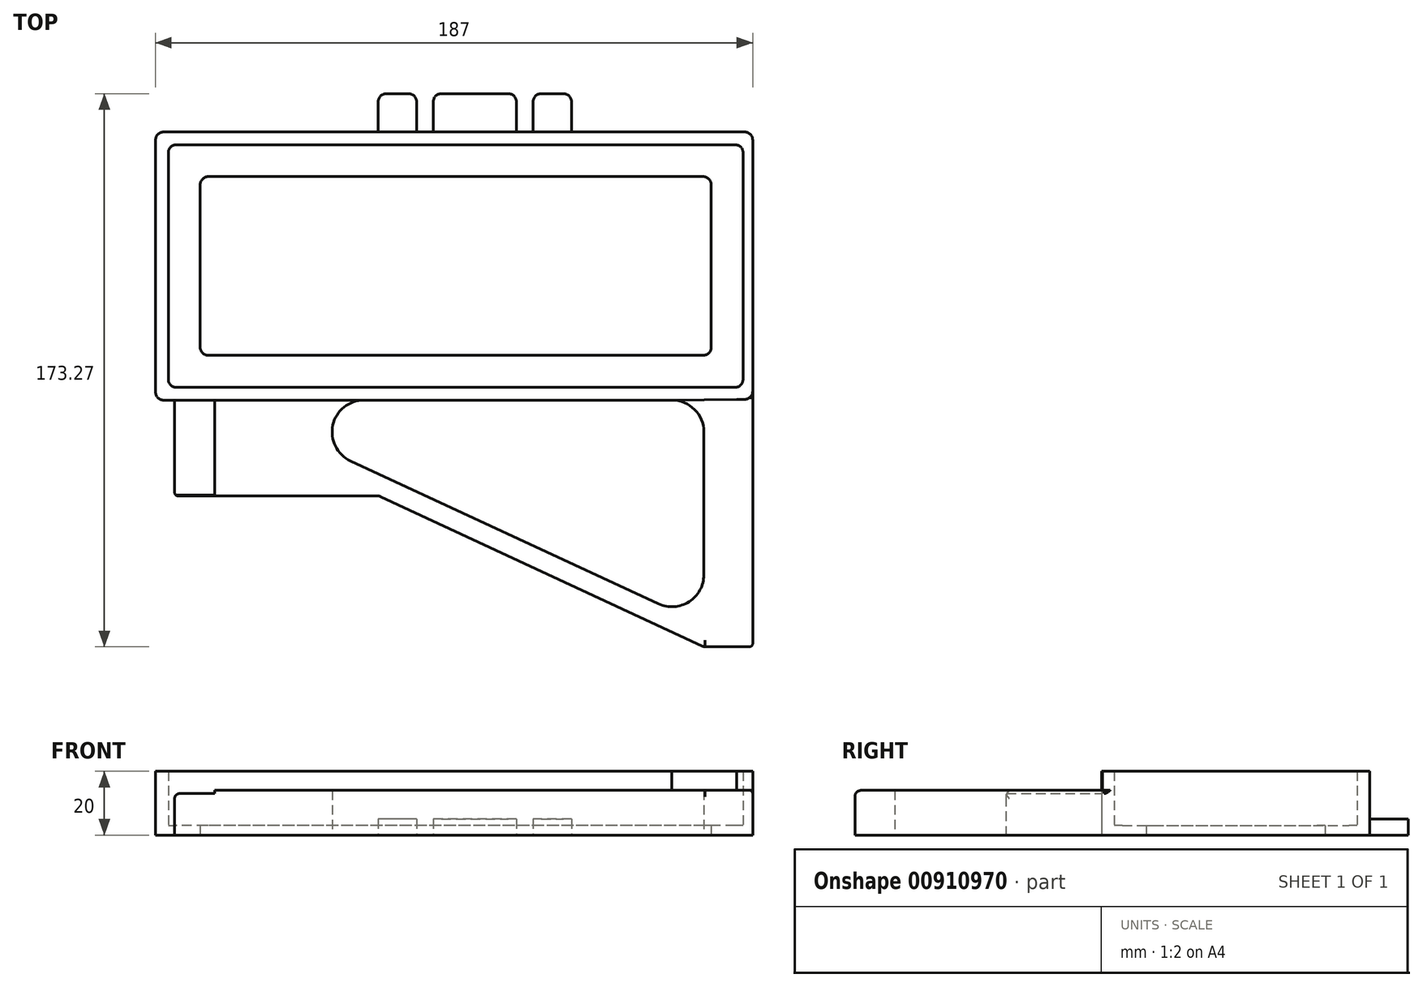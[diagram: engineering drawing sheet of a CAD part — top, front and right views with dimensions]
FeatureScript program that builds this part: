
annotation { "Feature Type Name" : "Feature", "Feature Type Description" : "" }
export const myFeature = defineFeature(function(context is Context, id is Id, definition is map)
    precondition{}
    {
        {
            var Q0;
            Q0=qCreatedBy(makeId("Top.planeOp"),FACE);
            var sketch = newSketch(context, id + "F0", { "sketchPlane" : qUnion([Q0])});
            skLineSegment(sketch, "E0.bottom", {"start": v(87.5, 0) * mm, "end": v(-87.5, 0) * mm});
            skLineSegment(sketch, "E0.top", {"start": v(87.5, 76) * mm, "end": v(-87.5, 76) * mm});
            skLineSegment(sketch, "E0.left", {"start": v(90, 2.5) * mm, "end": v(90, 73.5) * mm});
            skLineSegment(sketch, "E0.right", {"start": v(-90, 2.5) * mm, "end": v(-90, 73.5) * mm});
            skLineSegment(sketch, "E1.0", {"start": v(102, 80) * mm, "end": v(-74, 80) * mm});
            skLineSegment(sketch, "E2.0", {"start": v(-94, 0) * mm, "end": v(-94, 76) * mm});
            skLineSegment(sketch, "E3.0", {"start": v(67.7, -4) * mm, "end": v(-28.7, -4) * mm});
            skLineSegment(sketch, "E4.0", {"start": v(93, 0) * mm, "end": v(93, 76) * mm});
            skLineSegment(sketch, "E5", {"start": v(-74, 80) * mm, "end": v(-91.5, 80) * mm});
            skLineSegment(sketch, "E6", {"start": v(-94, 76) * mm, "end": v(-94, 77.5) * mm});
            skLineSegment(sketch, "E7", {"start": v(-94, -1.5) * mm, "end": v(-94, 0) * mm});
            skLineSegment(sketch, "E8", {"start": v(-88, -4) * mm, "end": v(-91.5, -4) * mm});
            skLineSegment(sketch, "E9", {"start": v(90.5, 80) * mm, "end": v(102, 80) * mm});
            skLineSegment(sketch, "E10", {"start": v(93, 77.5) * mm, "end": v(93, 76) * mm});
            skLineSegment(sketch, "E11", {"start": v(88, -3.77) * mm, "end": v(90.5, -3.77) * mm});
            skLineSegment(sketch, "E12", {"start": v(93, -1.27) * mm, "end": v(93, 0) * mm});
            skLineSegment(sketch, "E13", {"start": v(-7, 80) * mm, "end": v(-7, 89.5) * mm});
            skLineSegment(sketch, "E14", {"start": v(-4.5, 92) * mm, "end": v(16.5, 92) * mm});
            skLineSegment(sketch, "E15", {"start": v(19, 89.5) * mm, "end": v(19, 80) * mm});
            skLineSegment(sketch, "E16", {"start": v(6, 92) * mm, "end": v(6, 80) * mm, "construction": true});
            skLineSegment(sketch, "E17", {"start": v(6, 80) * mm, "end": v(6, 76) * mm, "construction": true});
            skLineSegment(sketch, "E18", {"start": v(-12.25, 80) * mm, "end": v(-12.25, 89.5) * mm});
            skLineSegment(sketch, "E19", {"start": v(-14.75, 92) * mm, "end": v(-21.75, 92) * mm});
            skLineSegment(sketch, "E20", {"start": v(-24.25, 89.5) * mm, "end": v(-24.25, 80) * mm});
            skLineSegment(sketch, "E21", {"start": v(24.25, 80) * mm, "end": v(24.25, 89.5) * mm});
            skLineSegment(sketch, "E22", {"start": v(26.75, 92) * mm, "end": v(33.75, 92) * mm});
            skLineSegment(sketch, "E23", {"start": v(36.25, 89.5) * mm, "end": v(36.25, 80) * mm});
            skPoint(sketch, "E24.visualSharp", {"position": v(19, 92) * mm});
            skArc(sketch, "E24.filletArc", {"start": v(19, 89.5) * mm, "mid": v(18.27, 91.27) * mm, "end": v(16.5, 92) * mm});
            skPoint(sketch, "E25.visualSharp", {"position": v(-7, 92) * mm});
            skArc(sketch, "E25.filletArc", {"start": v(-4.5, 92) * mm, "mid": v(-6.27, 91.27) * mm, "end": v(-7, 89.5) * mm});
            skPoint(sketch, "E26.visualSharp", {"position": v(-12.25, 92) * mm});
            skArc(sketch, "E26.filletArc", {"start": v(-12.25, 89.5) * mm, "mid": v(-12.98, 91.27) * mm, "end": v(-14.75, 92) * mm});
            skPoint(sketch, "E27.visualSharp", {"position": v(24.25, 92) * mm});
            skArc(sketch, "E27.filletArc", {"start": v(26.75, 92) * mm, "mid": v(24.98, 91.27) * mm, "end": v(24.25, 89.5) * mm});
            skPoint(sketch, "E28.visualSharp", {"position": v(-24.25, 92) * mm});
            skArc(sketch, "E28.filletArc", {"start": v(-21.75, 92) * mm, "mid": v(-23.52, 91.27) * mm, "end": v(-24.25, 89.5) * mm});
            skPoint(sketch, "E29.visualSharp", {"position": v(36.25, 92) * mm});
            skArc(sketch, "E29.filletArc", {"start": v(36.25, 89.5) * mm, "mid": v(35.52, 91.27) * mm, "end": v(33.75, 92) * mm});
            skPoint(sketch, "E30.visualSharp", {"position": v(-90, 76) * mm});
            skArc(sketch, "E30.filletArc", {"start": v(-87.5, 76) * mm, "mid": v(-89.27, 75.27) * mm, "end": v(-90, 73.5) * mm});
            skPoint(sketch, "E31.visualSharp", {"position": v(-94, 80) * mm});
            skArc(sketch, "E31.filletArc", {"start": v(-91.5, 80) * mm, "mid": v(-93.27, 79.27) * mm, "end": v(-94, 77.5) * mm});
            skPoint(sketch, "E32.visualSharp", {"position": v(-90, 0) * mm});
            skArc(sketch, "E32.filletArc", {"start": v(-90, 2.5) * mm, "mid": v(-89.27, 0.73) * mm, "end": v(-87.5, 0) * mm});
            skPoint(sketch, "E33.visualSharp", {"position": v(-94, -4) * mm});
            skArc(sketch, "E33.filletArc", {"start": v(-94, -1.5) * mm, "mid": v(-93.27, -3.27) * mm, "end": v(-91.5, -4) * mm});
            skPoint(sketch, "E34.visualSharp", {"position": v(93, -3.77) * mm});
            skArc(sketch, "E34.filletArc", {"start": v(90.5, -3.77) * mm, "mid": v(92.27, -3.03) * mm, "end": v(93, -1.27) * mm});
            skPoint(sketch, "E35.visualSharp", {"position": v(90, 0) * mm});
            skArc(sketch, "E35.filletArc", {"start": v(87.5, 0) * mm, "mid": v(89.27, 0.73) * mm, "end": v(90, 2.5) * mm});
            skPoint(sketch, "E36.visualSharp", {"position": v(90, 76) * mm});
            skArc(sketch, "E36.filletArc", {"start": v(90, 73.5) * mm, "mid": v(89.27, 75.27) * mm, "end": v(87.5, 76) * mm});
            skPoint(sketch, "E37.visualSharp", {"position": v(93, 80) * mm});
            skArc(sketch, "E37.filletArc", {"start": v(93, 77.5) * mm, "mid": v(92.27, 79.27) * mm, "end": v(90.5, 80) * mm});
            skLineSegment(sketch, "E38.0", {"start": v(77.5, 66) * mm, "end": v(-77.5, 66) * mm});
            skLineSegment(sketch, "E39.0", {"start": v(80, 12.5) * mm, "end": v(80, 63.5) * mm});
            skLineSegment(sketch, "E40.0", {"start": v(77.5, 10) * mm, "end": v(-77.5, 10) * mm});
            skLineSegment(sketch, "E41.0", {"start": v(-80, 12.5) * mm, "end": v(-80, 63.5) * mm});
            skPoint(sketch, "E42.visualSharp", {"position": v(-80, 66) * mm});
            skArc(sketch, "E42.filletArc", {"start": v(-77.5, 66) * mm, "mid": v(-79.27, 65.27) * mm, "end": v(-80, 63.5) * mm});
            skPoint(sketch, "E43.visualSharp", {"position": v(-80, 10) * mm});
            skArc(sketch, "E43.filletArc", {"start": v(-80, 12.5) * mm, "mid": v(-79.27, 10.73) * mm, "end": v(-77.5, 10) * mm});
            skPoint(sketch, "E44.visualSharp", {"position": v(80, 66) * mm});
            skArc(sketch, "E44.filletArc", {"start": v(80, 63.5) * mm, "mid": v(79.27, 65.27) * mm, "end": v(77.5, 66) * mm});
            skPoint(sketch, "E45.visualSharp", {"position": v(80, 10) * mm});
            skArc(sketch, "E45.filletArc", {"start": v(77.5, 10) * mm, "mid": v(79.27, 10.73) * mm, "end": v(80, 12.5) * mm});
            skLineSegment(sketch, "E46", {"start": v(93, -1.27) * mm, "end": v(93, -81.27) * mm});
            skLineSegment(sketch, "E47", {"start": v(93, -81.27) * mm, "end": v(77.65, -81.27) * mm});
            skLineSegment(sketch, "E48", {"start": v(-88, -4) * mm, "end": v(-88, -34) * mm});
            skLineSegment(sketch, "E49", {"start": v(-88, -34) * mm, "end": v(-75.5, -34) * mm});
            skLineSegment(sketch, "E50", {"start": v(-75.5, -34) * mm, "end": v(-75.5, -4) * mm});
            skLineSegment(sketch, "E51", {"start": v(-23.52, -34.23) * mm, "end": v(77.65, -81.27) * mm});
            skLineSegment(sketch, "E52", {"start": v(63.5, -67.8) * mm, "end": v(-32.9, -23.07) * mm});
            skArc(sketch, "E53.filletArc", {"start": v(77.7, -14) * mm, "mid": v(74.78, -6.93) * mm, "end": v(67.7, -4) * mm});
            skLineSegment(sketch, "E54", {"start": v(67.7, -4) * mm, "end": v(88, -3.77) * mm});
            skLineSegment(sketch, "E55", {"start": v(77.7, -14) * mm, "end": v(77.7, -58.74) * mm});
            skLineSegment(sketch, "E56", {"start": v(77.65, -74.17) * mm, "end": v(77.65, -81.27) * mm});
            skArc(sketch, "E57.filletArc", {"start": v(63.5, -67.8) * mm, "mid": v(73.09, -67.17) * mm, "end": v(77.7, -58.74) * mm});
            skPoint(sketch, "E58.newPointA", {"position": v(-88, -4) * mm});
            skArc(sketch, "E58.filletArc", {"start": v(-28.7, -4) * mm, "mid": v(-38.46, -11.84) * mm, "end": v(-32.9, -23.07) * mm});
            skLineSegment(sketch, "E59", {"start": v(-28.7, -4) * mm, "end": v(-88, -4) * mm});
            skLineSegment(sketch, "E60", {"start": v(6, 76) * mm, "end": v(6, -4) * mm, "construction": true});
            skLineSegment(sketch, "E61", {"start": v(-75.5, -34) * mm, "end": v(-24.57, -34) * mm});
            skArc(sketch, "E62.filletArc", {"start": v(-23.52, -34.23) * mm, "mid": v(-24.03, -34.06) * mm, "end": v(-24.57, -34) * mm});
            skSolve(sketch);
        }
        {
            var Q0;
            Q0=makeQuery(id+"F0.imprint","IMPRINT",FACE,{"disambiguationData":[TD([[makeQuery(id+"F0.imprint","IMPRINT",EDGE,{"derivedFrom":sQuery(id+"F0.wireOp",EDGE,"E0.bottom")}),1.0]])]});
            extrude(context, id + "F1", {"entities" : qUnion([Q0]), "depth" : 20 * mm, "offsetDistance" : 25 * mm});
        }
        {
            var Q0;
            Q0=makeQuery(id+"F0.imprint","IMPRINT",FACE,{"disambiguationData":[TD([[makeQuery(id+"F0.imprint","IMPRINT",EDGE,{"derivedFrom":sQuery(id+"F0.wireOp",EDGE,"E0.bottom")}),-1.0]])]});
            extrude(context, id + "F2", {"entities" : qUnion([Q0]), "operationType" : NewBodyOperationType.ADD, "depth" : 3 * mm, "offsetDistance" : 25 * mm});
        }
        {
            var Q0;
            {var subQ0=sQuery(id+"F0.wireOp",EDGE,"E11");Q0=makeQuery(id+"F0.imprint","IMPRINT",FACE,{"disambiguationData":[TD([[makeQuery(id+"F0.imprint","IMPRINT",EDGE,{"derivedFrom":subQ0}),-1.0]])]});}
            var Q1;
            {var subQ0=sQuery(id+"F0.wireOp",EDGE,"E47");Q1=makeQuery(id+"F0.imprint","IMPRINT",FACE,{"disambiguationData":[TD([[makeQuery(id+"F0.imprint","IMPRINT",EDGE,{"derivedFrom":subQ0}),-1.0]])]});}
            extrude(context, id + "F3", {"entities" : qUnion([Q0, Q1]), "operationType" : NewBodyOperationType.ADD, "depth" : 14 * mm, "offsetDistance" : 25 * mm});
        }
        {
            var Q0;
            {var subQ1=sQuery(id+"F0.wireOp",EDGE,"Ny0Gnn2i-Ygqb-VPq2-N1I1-QU3OLZ8xniGR");var subQ3=sQuery(id+"F0.wireOp",EDGE,"E52");var subQ4=makeQuery(id+"F0.imprint","INTERSECT",VERTEX,{"derivedFrom":[subQ1,subQ3]});Q0=makeQuery(id+"F0.imprint","IMPRINT",FACE,{"disambiguationData":[TD([[makeQuery(id+"F0.imprint","IMPRINT",EDGE,{"disambiguationData":[TD([[subQ4,1.0]])],"derivedFrom":subQ1}),1.0]])]});}
            var Q1;
            {var subQ0=sQuery(id+"F0.wireOp",EDGE,"E59");var subQ5=sQuery(id+"F0.wireOp",EDGE,"E50");var subQ6=makeQuery(id+"F0.imprint","INTERSECT",VERTEX,{"derivedFrom":[subQ5,subQ0]});Q1=makeQuery(id+"F0.imprint","IMPRINT",FACE,{"disambiguationData":[TD([[makeQuery(id+"F0.imprint","IMPRINT",EDGE,{"disambiguationData":[TD([[subQ6,1.0]])],"derivedFrom":subQ5}),1.0]])]});}
            var Q2;
            {var subQ0=sQuery(id+"F0.wireOp",EDGE,"fGbPgxKb-3OdY-1Y91-8G2S-CM4cBlenFRyz");Q2=makeQuery(id+"F0.imprint","IMPRINT",FACE,{"disambiguationData":[TD([[makeQuery(id+"F0.imprint","IMPRINT",EDGE,{"derivedFrom":subQ0}),1.0]])]});}
            var Q3;
            {var subQ0=sQuery(id+"F0.wireOp",EDGE,"E48");Q3=makeQuery(id+"F0.imprint","IMPRINT",FACE,{"disambiguationData":[TD([[makeQuery(id+"F0.imprint","IMPRINT",EDGE,{"derivedFrom":subQ0}),1.0]])]});}
            extrude(context, id + "F4", {"entities" : qUnion([Q0, Q1, Q2, Q3]), "operationType" : NewBodyOperationType.ADD, "depth" : 13 * mm, "offsetDistance" : 25 * mm});
        }
        {
            var Q0;
            Q0=makeQuery(id+"F3.opExtrude","CAP_EDGE",EDGE,{"disambiguationData":[OSD([sQuery(id+"F0.wireOp",EDGE,"E47")])],"isStart":false});
            fillet(context, id + "F5", {"entities" : qUnion([Q0]), "radius" : 2 * mm, "tangentPropagation" : true, "allowEdgeOverflow" : false});
        }
        {
            var Q0;
            Q0=makeQuery(id+"F3.opExtrude","CAP_EDGE",EDGE,{"disambiguationData":[OSD([sQuery(id+"F0.wireOp",EDGE,"E51")])],"isStart":false});
            fillet(context, id + "F6", {"entities" : qUnion([Q0]), "radius" : 2 * mm, "tangentPropagation" : true, "allowEdgeOverflow" : false});
        }
        {
            var Q0;
            Q0=makeQuery(id+"F3.opExtrude","SWEPT_EDGE",EDGE,{"disambiguationData":[OSD([sQuery(id+"F0.wireOp",EDGE,"E46"),sQuery(id+"F0.wireOp",EDGE,"E47")])]});
            fillet(context, id + "F7", {"entities" : qUnion([Q0]), "radius" : 1 * mm, "tangentPropagation" : true, "allowEdgeOverflow" : false});
        }
        {
            var Q0;
            Q0=makeQuery(id+"F4.opExtrude","SWEPT_EDGE",EDGE,{"disambiguationData":[OSD([sQuery(id+"F0.wireOp",EDGE,"E48"),sQuery(id+"F0.wireOp",EDGE,"E49")])]});
            fillet(context, id + "F8", {"entities" : qUnion([Q0]), "radius" : 1 * mm, "tangentPropagation" : true, "allowEdgeOverflow" : false});
        }
        {
            var Q0;
            {var subQ1=sQuery(id+"F0.wireOp",EDGE,"E18");Q0=makeQuery(id+"F0.imprint","IMPRINT",FACE,{"disambiguationData":[TD([[makeQuery(id+"F0.imprint","IMPRINT",EDGE,{"derivedFrom":subQ1}),1.0]])]});}
            var Q1;
            {var subQ1=sQuery(id+"F0.wireOp",EDGE,"E13");Q1=makeQuery(id+"F0.imprint","IMPRINT",FACE,{"disambiguationData":[TD([[makeQuery(id+"F0.imprint","IMPRINT",EDGE,{"derivedFrom":subQ1}),-1.0]])]});}
            var Q2;
            {var subQ1=sQuery(id+"F0.wireOp",EDGE,"E21");Q2=makeQuery(id+"F0.imprint","IMPRINT",FACE,{"disambiguationData":[TD([[makeQuery(id+"F0.imprint","IMPRINT",EDGE,{"derivedFrom":subQ1}),-1.0]])]});}
            extrude(context, id + "F9", {"entities" : qUnion([Q0, Q1, Q2]), "operationType" : NewBodyOperationType.ADD, "depth" : 5 * mm, "offsetDistance" : 25 * mm});
        }
        {
            var Q0;
            Q0=makeQuery(id+"F4.opExtrude","CAP_EDGE",EDGE,{"disambiguationData":[OSD([sQuery(id+"F0.wireOp",EDGE,"E48")])],"isStart":false});
            fillet(context, id + "F10", {"entities" : qUnion([Q0]), "radius" : 1.5 * mm, "tangentPropagation" : true, "allowEdgeOverflow" : false});
        }
    });
